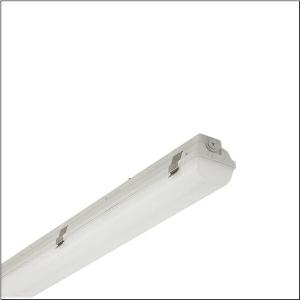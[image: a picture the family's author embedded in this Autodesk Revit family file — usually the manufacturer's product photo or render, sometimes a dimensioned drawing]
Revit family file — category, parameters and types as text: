
# Revit family: monsun_r__21_eco_51fj10dl45a_5ac6
name_source: partatom
category: Lighting Fixtures
units: mm (PartAtom-declared; Revit-internal decimal feet)

## family parameters
Cut with Voids When Loaded = No
Host = Face
Light Source = No
Part Type = Normal
Room Calculation Point = No
Round Connector Dimension = Use Diameter
Shared = No

## types (1)
- Monsun® 21 Eco (1 x LED, 5100 lm, 36 W, 4000K)
    Apparent Load = 36 VA
    CIE Flux Codes = 41 70 89 90 100
    Color Rendering = 80
    Color Temperature = 4000K
    Default Elevation = 1800 mm
    Description = Monsun® 21 Eco, damp-proof luminaire, primary optical cover: diffuser, of PMMA, frosted, light emission: direct distribution, primary light characteristic: symmetric, installation type: suspended mounting, surface-mounted, LED, rated luminous flux: 5.100lm, luminous efficacy: 142lm/W, light colour: 840, colour temperature: 4000K, control gear: ECG DALI, with terminal, 5-pole, max. 2.5mm², mains connection: 220..240V, AC, 50/60Hz, rated input power: 36W, housing, of glass-fibre reinforced polyester, light grey (RAL 7035), length: 1.277mm, width: 90mm, height: 95mm, clip for enclosure, of spring steel V2A, protection rating (complete): IP66, insulation class (complete): insulation class I (protective earthing), certification: CE, UKCA, protection symbol: D, impact resistance: IK02, permissible operating ambient temperature: -20..+35°C, corresponds to IFS (International Featured Standards) requirements for safety and quality in the food industry, contact your sales advisor before using the luminaires in applications with unclear chemical exposure, large temperature fluctuations or condensation-forming humidity, packaging unit: 1 piece
    Height = 103 mm
    Lamp = 1 x LED
    Lamp Light Flux = 5100 lm
    Lamp Power = 36 W
    Lamp count = 1
    Length = 1277 mm
    Luminous efficacy = 142 lm/W
    Manufacturer = Siteco
    ModVariant = No
    Model = 51FJ10DL45A
    Mounting Place = Ceiling
    Mounting Type = Surface mounted
    Number of Poles = 1
    OnlyDefault = Yes
    Power Factor = 1
    Product Name = Monsun® 21 Eco
    Product group = damp-proof luminaire
    ProductGroupID = 300
    Protection Class = Protection class I
    Protection Degree = IP 66
    RLX_Detail_Level = 1
    RLX_Emergency_Light_Flux = 0 lm
    RLX_Emergency_Type = 0
    RLX_Emergency_Type_DB = No
    RlxData = <blob elided: 33421 chars, md5=ac217ae3>
    Socket = socket
    Standby Power = 0 W
    System Light Flux = 5100 lm
    System Power = 36 W
    Type Comments = Product without accessories
    Type Image = l_1007218.jpg
    URL = http://relux.com
    VarID = ---
    Voltage = 0 V
    Weight = 0.00 kg
    Width = 90 mm

## geometry (parser evidence)
native form markers: Blend x4, Sweep x14
no freeform markers — native parametric forms only
